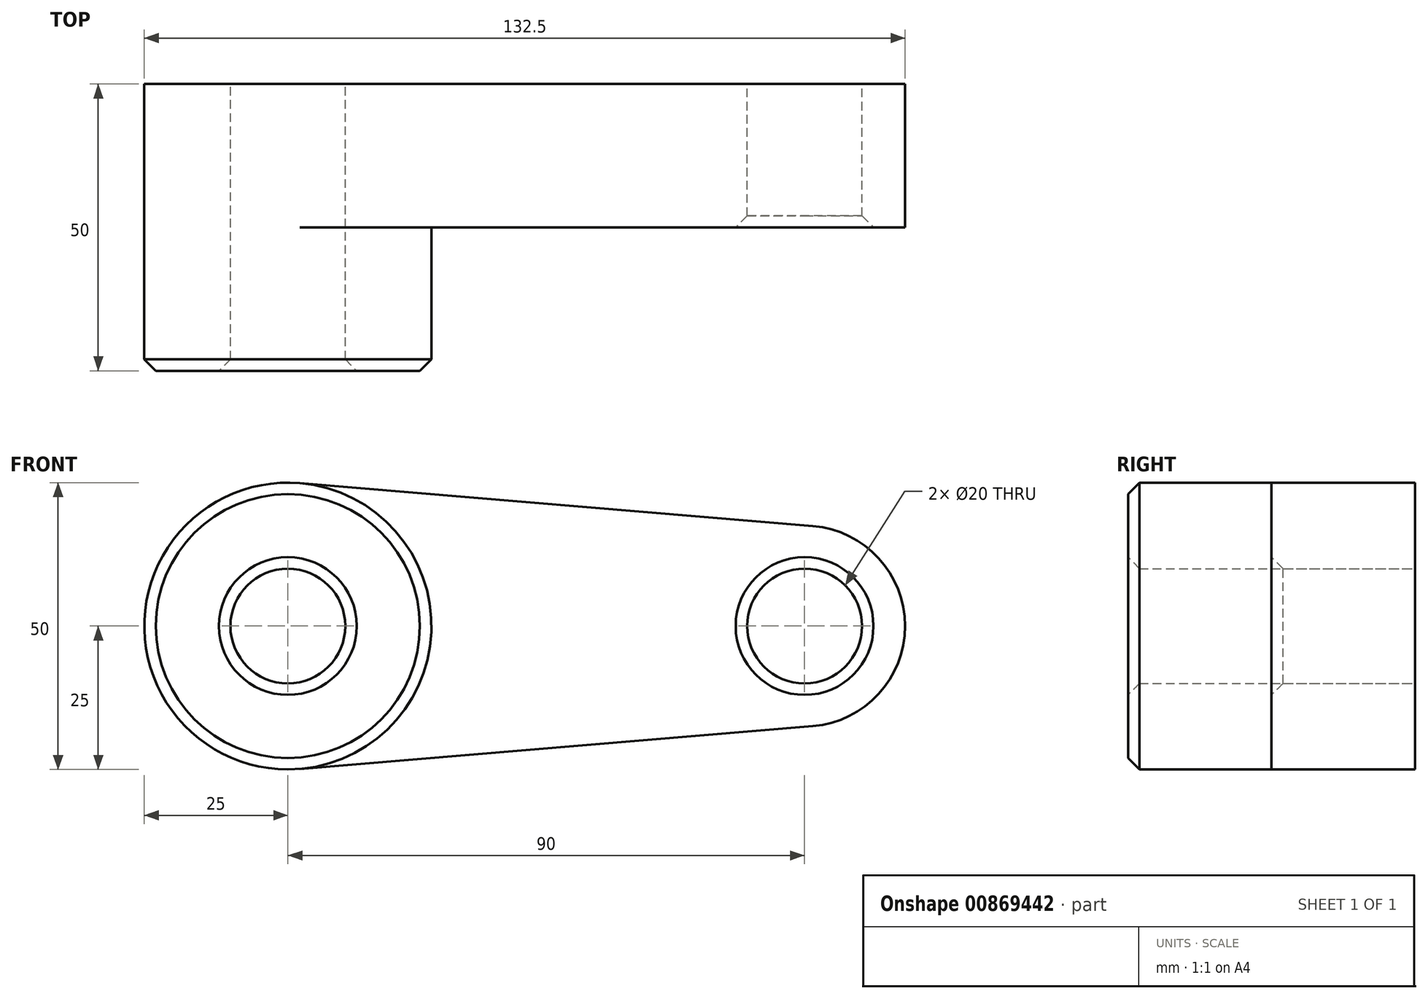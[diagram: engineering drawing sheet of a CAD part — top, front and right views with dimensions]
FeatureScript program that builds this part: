
annotation { "Feature Type Name" : "Feature", "Feature Type Description" : "" }
export const myFeature = defineFeature(function(context is Context, id is Id, definition is map)
    precondition{}
    {
        {
            var Q0;
            Q0=qCreatedBy(makeId("Front.planeOp"),FACE);
            var sketch = newSketch(context, id + "F0", { "sketchPlane" : qUnion([Q0])});
            skCircle(sketch, "E0", {"center": v(0, 0) * mm, "radius": 25 * mm});
            skCircle(sketch, "E1", {"center": v(90, 0) * mm, "radius": 17.5 * mm});
            skLineSegment(sketch, "E2", {"start": v(2.08, 24.91) * mm, "end": v(91.46, 17.44) * mm});
            skLineSegment(sketch, "E3", {"start": v(2.08, -24.91) * mm, "end": v(91.46, -17.44) * mm});
            skCircle(sketch, "E4", {"center": v(0, 0) * mm, "radius": 10 * mm});
            skCircle(sketch, "E5", {"center": v(90, 0) * mm, "radius": 10 * mm});
            skSolve(sketch);
        }
        {
            var Q0;
            Q0=qSketchRegion(id+"F0",true);
            extrude(context, id + "F1", {"entities" : qUnion([Q0]), "depth" : 25 * mm});
        }
        {
            var Q0;
            Q0=makeQuery(id+"F0.imprint","IMPRINT",FACE,{"disambiguationData":[TD([[makeQuery(id+"F0.imprint","IMPRINT",EDGE,{"derivedFrom":sQuery(id+"F0.wireOp",EDGE,"E4")}),-1.0]])]});
            extrude(context, id + "F2", {"entities" : qUnion([Q0]), "operationType" : NewBodyOperationType.ADD, "depth" : 50 * mm});
        }
        {
            var Q0;
            Q0=makeQuery(id+"F2.opExtrude","CAP_EDGE",EDGE,{"disambiguationData":[OSD([sQuery(id+"F0.wireOp",EDGE,"E0")])],"isStart":false});
            var Q1;
            Q1=makeQuery(id+"F2.opExtrude","CAP_EDGE",EDGE,{"disambiguationData":[OSD([sQuery(id+"F0.wireOp",EDGE,"E4")])],"isStart":false});
            var Q2;
            Q2=makeQuery(id+"F1.opExtrude","CAP_EDGE",EDGE,{"disambiguationData":[OSD([sQuery(id+"F0.wireOp",EDGE,"E5")])],"isStart":false});
            chamfer(context, id + "F3", {"entities" : qUnion([Q0, Q1, Q2]), "width" : 2 * mm, "tangentPropagation" : true});
        }
        {
            var Q0;
            Q0=qCreatedBy(makeId("Front.planeOp"),FACE);
            var sketch = newSketch(context, id + "F4", { "sketchPlane" : qUnion([Q0])});
            skLineSegment(sketch, "E6", {"start": v(18.93, 0) * mm, "end": v(71.19, 47.64) * mm});
            skLineSegment(sketch, "E7", {"start": v(71.19, 47.64) * mm, "end": v(61.74, 0) * mm});
            skSolve(sketch);
        }
        {
            var Q0;
            Q0=makeQuery(id+"F1.opExtrude","CAP_FACE",FACE,{"disambiguationData":[OSD([sQuery(id+"F0.wireOp",EDGE,"E0"),sQuery(id+"F0.wireOp",EDGE,"E1"),sQuery(id+"F0.wireOp",EDGE,"E2"),sQuery(id+"F0.wireOp",EDGE,"E3"),sQuery(id+"F0.wireOp",EDGE,"E4"),sQuery(id+"F0.wireOp",EDGE,"E5")])],"isStart":false});
            var Q1;
            Q1=sQuery(id+"F4.wireOp",EDGE,"E6");
            var Q2;
            Q2=sQuery(id+"F4.wireOp",EDGE,"E7");
            extrude(context, id + "F5", {"entities" : qUnion([Q0]), "bodyType" : ToolBodyType.SURFACE, "operationType" : NewBodyOperationType.ADD, "surfaceEntities" : qUnion([Q1, Q2]), "depth" : 25 * mm, "offsetDistance" : 25 * mm});
        }
    });
